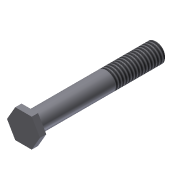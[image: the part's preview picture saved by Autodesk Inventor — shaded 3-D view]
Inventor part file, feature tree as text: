
AUTODESK INVENTOR PART (.ipt)
format: ipt  version: 2011 (Build 150239000, 239)  size: 92,672 bytes
history: native  units: in
note: dims shown in document units (in); Inventor stores cm internally (conversion verified against a paired STEP export)
features: extrude x2, sketch x2, thread x1, chamfer x1
ambient origin geometry x8: Origin, YZ Plane, XZ Plane, XY Plane, X Axis, Y Axis, Z Axis, Center Point
bodies: Solid1 (feature_tree)
feature tree (6):
  extrude  "Extrusion1"  Depth=2.5in TaperAngle=0.0deg
  extrude  "Extrusion2"  Depth=0.125in TaperAngle=0.0deg
  thread  "Thread1"  [1 undecoded]
  chamfer  "Chamfer1"  Distance=0.02in Angle=45.0deg
  sketch  "Sketch1"  dims[d0=0.375in d1=2.5in d2=0.0in]
  sketch  "Sketch2"  dims[d3=0.5625in d4=0.125in d5=0.0in d6=1.0in d7=0.0in d8=0.02in d9=0.125in d10=45.0deg]
note: 1 required parameter value undecoded (feature->parameter linkage not recoverable at this tier; creation-order binding heuristic only, values carry confidence <= 0.55)
